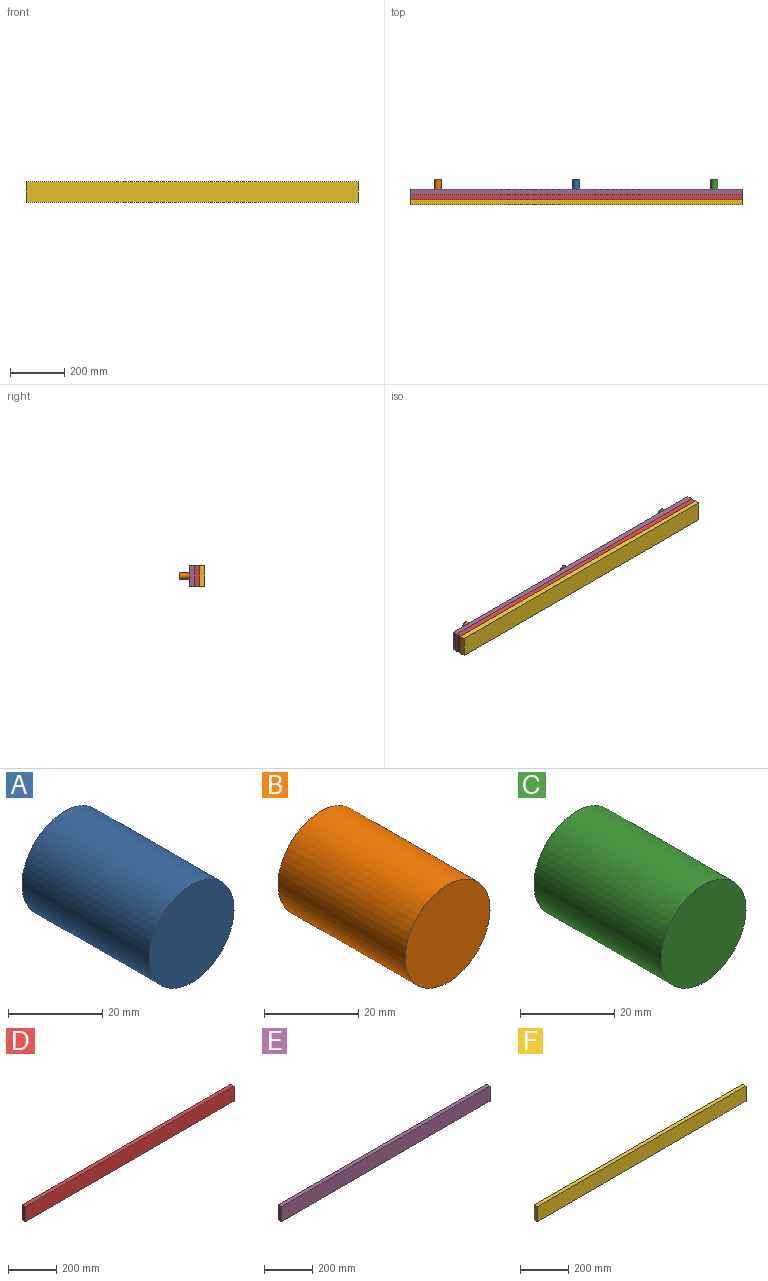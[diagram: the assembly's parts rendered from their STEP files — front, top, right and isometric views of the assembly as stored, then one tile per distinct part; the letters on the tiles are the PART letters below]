
ASSEMBLY  parts=6 mates=5
PART A: 3 faces, bbox 25.4x38.1x25.4 mm
  f0: cylinder r=12.7mm len=38.1mm, axis (0,-1,0), area 3040.2mm2, adj f1,f2
  f1: plane 25.4x25.4mm, normal (0,1,0), area 506.7mm2, adj f0
  f2: plane 25.4x25.4mm, normal (0,-1,0), area 506.7mm2, adj f0
PART B: 3 faces, bbox 25.4x38.1x25.4 mm
  f0: cylinder r=12.7mm len=38.1mm, axis (0,-1,0), area 3040.2mm2, adj f1,f2
  f1: plane 25.4x25.4mm, normal (0,1,0), area 506.7mm2, adj f0
  f2: plane 25.4x25.4mm, normal (0,-1,0), area 506.7mm2, adj f0
PART C: 3 faces, bbox 25.4x38.1x25.4 mm
  f0: cylinder r=12.7mm len=38.1mm, axis (0,-1,0), area 3040.2mm2, adj f1,f2
  f1: plane 25.4x25.4mm, normal (0,1,0), area 506.7mm2, adj f0
  f2: plane 25.4x25.4mm, normal (0,-1,0), area 506.7mm2, adj f0
PART D: 6 faces, bbox 1219.2x19.1x76.2 mm
  f0: plane 1219.2x19.05mm, normal (0,0,1), area 23225.8mm2, adj f1,f3,f4,f5
  f1: plane 76.2x19.05mm, normal (-1,0,0), area 1451.6mm2, adj f0,f2,f4,f5
  f2: plane 1219.2x19.05mm, normal (0,0,-1), area 23225.8mm2, adj f1,f3,f4,f5
  f3: plane 76.2x19.05mm, normal (1,0,0), area 1451.6mm2, adj f0,f2,f4,f5
  f4: plane 1219.2x76.2mm, normal (0,1,0), area 92903mm2, adj f0,f1,f2,f3
  f5: plane 1219.2x76.2mm, normal (0,-1,0), area 92903mm2, adj f0,f1,f2,f3
PART E: 6 faces, bbox 1219.2x19.1x76.2 mm
  f0: plane 1219.2x19.05mm, normal (0,0,1), area 23225.8mm2, adj f1,f3,f4,f5
  f1: plane 76.2x19.05mm, normal (-1,0,0), area 1451.6mm2, adj f0,f2,f4,f5
  f2: plane 1219.2x19.05mm, normal (0,0,-1), area 23225.8mm2, adj f1,f3,f4,f5
  f3: plane 76.2x19.05mm, normal (1,0,0), area 1451.6mm2, adj f0,f2,f4,f5
  f4: plane 1219.2x76.2mm, normal (0,1,0), area 92903mm2, adj f0,f1,f2,f3
  f5: plane 1219.2x76.2mm, normal (0,-1,0), area 92903mm2, adj f0,f1,f2,f3
PART F: 6 faces, bbox 1219.2x19.1x76.2 mm
  f0: plane 1219.2x19.05mm, normal (0,0,1), area 23225.8mm2, adj f1,f3,f4,f5
  f1: plane 76.2x19.05mm, normal (-1,0,0), area 1451.6mm2, adj f0,f2,f4,f5
  f2: plane 1219.2x19.05mm, normal (0,0,-1), area 23225.8mm2, adj f1,f3,f4,f5
  f3: plane 76.2x19.05mm, normal (1,0,0), area 1451.6mm2, adj f0,f2,f4,f5
  f4: plane 1219.2x76.2mm, normal (0,1,0), area 92903mm2, adj f0,f1,f2,f3
  f5: plane 1219.2x76.2mm, normal (0,-1,0), area 92903mm2, adj f0,f1,f2,f3
PLACE A t=(0,-189.48,0)mm
PLACE B t=(0,-189.48,0)mm
PLACE C rot(axis=(0,-1,0),90deg) t=(466.81,-189.48,-772.93)mm
PLACE D t=(0,-189.46,0)mm
PLACE E t=(0,-189.48,0)mm
PLACE F t=(0,-189.43,0)mm
MATE fastened A.f0 <-> E.f4  axis (0,-1,0) through (111.87,-132.28,-153.06)mm
MATE fastened B.f0 <-> E.f4  axis (0,-1,0) through (-396.13,-132.28,-153.06)mm
MATE fastened F.f4 <-> D.f5  axis (0,1,0) through (111.87,-170.38,-153.06)mm
MATE fastened D.f4 <-> E.f5  axis (0,1,0) through (111.87,-151.33,-153.06)mm
MATE fastened C.f0 <-> E.f4  axis (0,-1,0) through (619.87,-132.28,-153.06)mm
